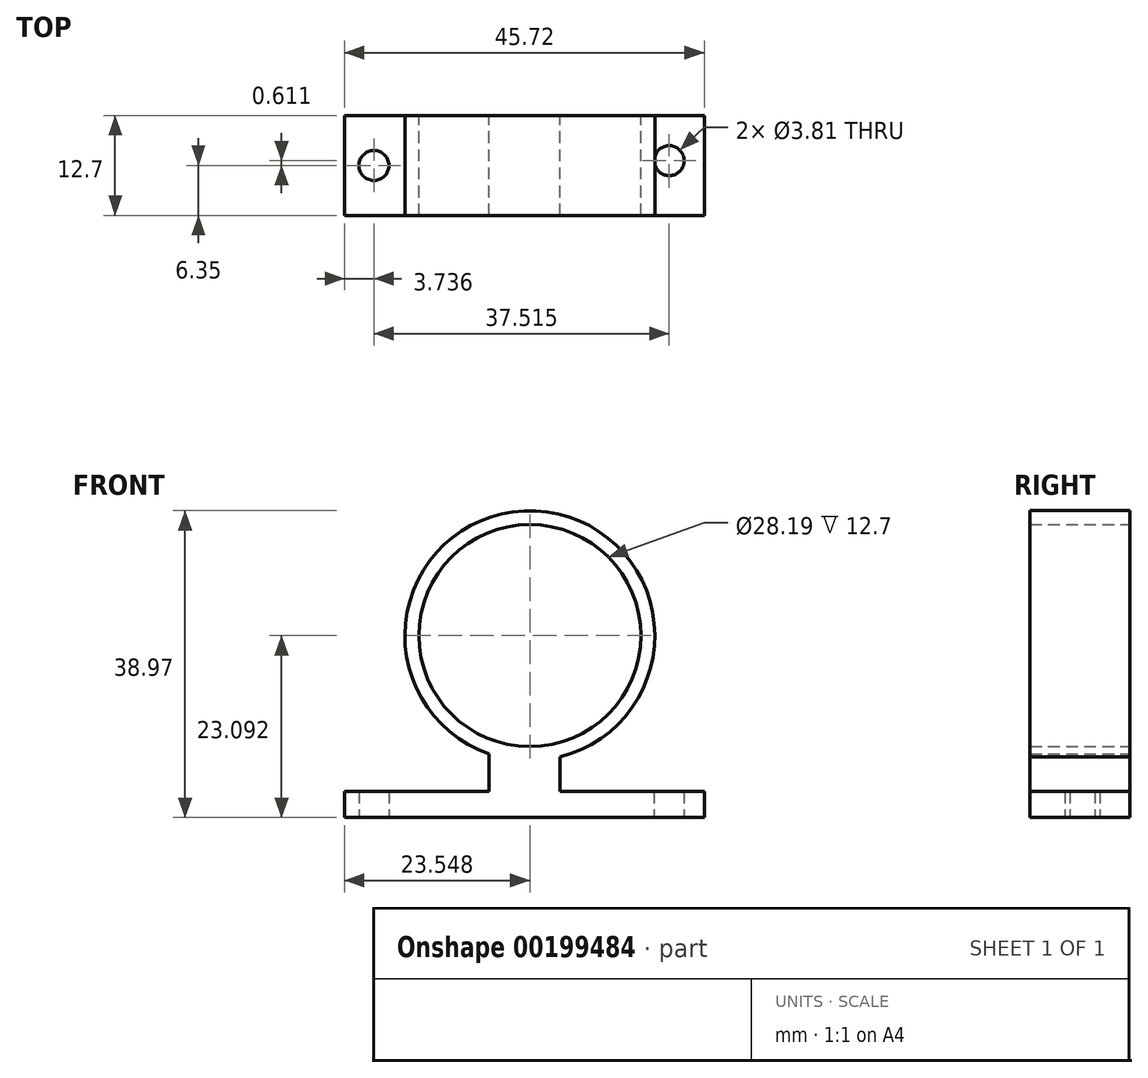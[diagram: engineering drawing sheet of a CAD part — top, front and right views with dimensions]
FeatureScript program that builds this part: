
annotation { "Feature Type Name" : "Feature", "Feature Type Description" : "" }
export const myFeature = defineFeature(function(context is Context, id is Id, definition is map)
    precondition{}
    {
        {
            var Q0;
            Q0=qCreatedBy(makeId("Front.planeOp"),FACE);
            var sketch = newSketch(context, id + "F0", { "sketchPlane" : qUnion([Q0])});
            skCircle(sketch, "E0", {"center": v(-48.14, 44.47) * mm, "radius": 15.88 * mm});
            skCircle(sketch, "E1", {"center": v(-48.14, 44.47) * mm, "radius": 14.1 * mm});
            skLineSegment(sketch, "E2.right", {"start": v(148.82, 28.6) * mm, "end": v(148.82, -0.93) * mm});
            skLineSegment(sketch, "E3.left", {"start": v(148.82, -0.93) * mm, "end": v(148.82, -0.93) * mm});
            skLineSegment(sketch, "E3.right", {"start": v(-48.93, -0.93) * mm, "end": v(-48.93, -0.93) * mm});
            skPoint(sketch, "E4.start.orphan", {"position": v(-15.5, -0.93) * mm});
            skPoint(sketch, "E5.start.orphan", {"position": v(-61.23, -0.93) * mm});
            skLineSegment(sketch, "E6.bottom", {"start": v(-53.36, 29.48) * mm, "end": v(-44.31, 29.48) * mm});
            skLineSegment(sketch, "E6.top", {"start": v(-53.36, 23.03) * mm, "end": v(-44.31, 23.03) * mm});
            skLineSegment(sketch, "E6.left", {"start": v(-53.36, 29.48) * mm, "end": v(-53.36, 23.03) * mm});
            skLineSegment(sketch, "E6.right", {"start": v(-44.31, 29.48) * mm, "end": v(-44.31, 23.03) * mm});
            skLineSegment(sketch, "E7.bottom", {"start": v(-71.7, 24.68) * mm, "end": v(-25.97, 24.68) * mm});
            skLineSegment(sketch, "E7.top", {"start": v(-71.7, 21.38) * mm, "end": v(-25.97, 21.38) * mm});
            skLineSegment(sketch, "E7.left", {"start": v(-71.7, 24.68) * mm, "end": v(-71.7, 21.38) * mm});
            skLineSegment(sketch, "E7.right", {"start": v(-25.97, 24.68) * mm, "end": v(-25.97, 21.38) * mm});
            skPoint(sketch, "E7.middle", {"position": v(-48.83, 23.03) * mm});
            skSolve(sketch);
        }
        {
            var Q0;
            Q0 = qSketchRegion(id + "F0", true);
            extrude(context, id + "F1", {"entities" : qUnion([Q0]), "depth" : 12.7 * mm});
        }
        {
            var Q0;
            Q0=makeQuery(id+"F1.opExtrude","SWEPT_FACE",FACE,{"disambiguationData":[OSD([sQuery(id+"F0.wireOp",EDGE,"E7.top")])]});
            var sketch = newSketch(context, id + "F2", { "sketchPlane" : qUnion([Q0])});
            skCircle(sketch, "E8", {"center": v(-67.95, 6.35) * mm, "radius": 1.9 * mm});
            skPoint(sketch, "E8.centerSnap0", {"position": v(-71.7, 6.35) * mm});
            skCircle(sketch, "E9.MirrorC", {"center": v(-30.44, 5.74) * mm, "radius": 1.9 * mm});
            skSolve(sketch);
        }
        {
            var Q0;
            Q0 = qSketchRegion(id + "F2", true);
            extrude(context, id + "F3", {"entities" : qUnion([Q0]), "operationType" : NewBodyOperationType.REMOVE, "oppositeDirection" : true, "depth" : 9.9 * mm});
        }
    });
